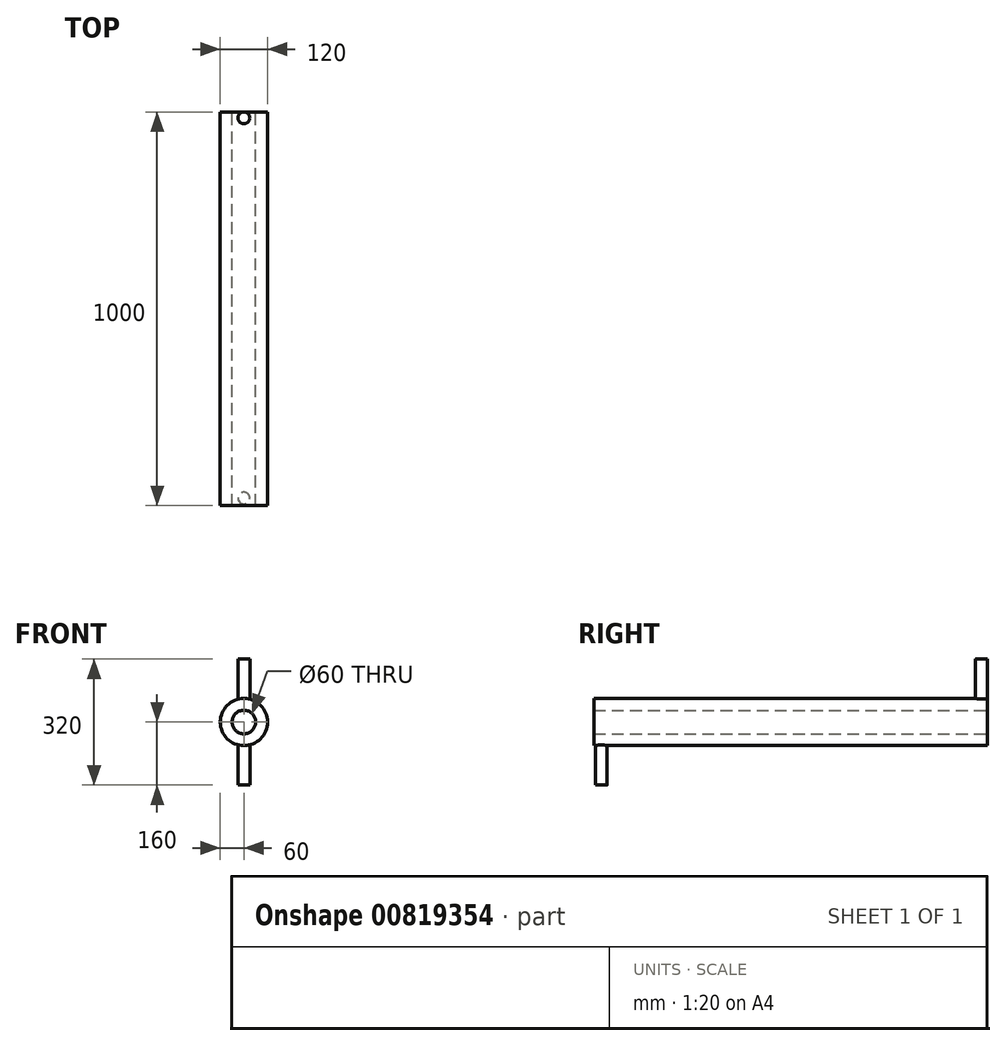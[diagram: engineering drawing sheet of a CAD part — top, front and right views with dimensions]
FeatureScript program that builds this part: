
annotation { "Feature Type Name" : "Feature", "Feature Type Description" : "" }
export const myFeature = defineFeature(function(context is Context, id is Id, definition is map)
    precondition{}
    {
        {
            var Q0;
            Q0=qCreatedBy(makeId("Front.planeOp"),FACE);
            var sketch = newSketch(context, id + "F0", { "sketchPlane" : qUnion([Q0])});
            skCircle(sketch, "E0", {"center": v(0, 0) * mm, "radius": 60 * mm});
            skCircle(sketch, "E1", {"center": v(0, 0) * mm, "radius": 30 * mm});
            skSolve(sketch);
        }
        {
            var Q0;
            Q0=makeQuery(id+"F0.imprint","IMPRINT",FACE,{"disambiguationData":[TD([[makeQuery(id+"F0.imprint","IMPRINT",EDGE,{"derivedFrom":sQuery(id+"F0.wireOp",EDGE,"E0")}),1.0]])]});
            extrude(context, id + "F1", {"entities" : qUnion([Q0]), "depth" : 1000 * mm, "offsetDistance" : 25 * mm});
        }
        {
            var Q0;
            Q0=qCreatedBy(makeId("Top.planeOp"),FACE);
            cPlane(context, id + "F2", {"entities" : qUnion([Q0]), "cplaneType" : CPlaneType.OFFSET, "offset" : 60 * mm, "width" : 150 * mm, "height" : 150 * mm});
        }
        {
            var Q0;
            Q0=qCreatedBy(id+"F2.planeOp",FACE);
            var sketch = newSketch(context, id + "F3", { "sketchPlane" : qUnion([Q0])});
            skCircle(sketch, "E2", {"center": v(0, -15) * mm, "radius": 15 * mm});
            skSolve(sketch);
        }
        {
            var Q0;
            Q0=makeQuery(id+"F3.imprint","IMPRINT",FACE,{"disambiguationData":[TD([[makeQuery(id+"F3.imprint","IMPRINT",EDGE,{"derivedFrom":sQuery(id+"F3.wireOp",EDGE,"E2")}),1.0]])]});
            var Q1;
            Q1=sQuery(id+"F3.wireOp",EDGE,"E2");
            extrude(context, id + "F4", {"entities" : qUnion([Q0]), "operationType" : NewBodyOperationType.ADD, "surfaceEntities" : qUnion([Q1]), "depth" : 100 * mm, "offsetDistance" : 25 * mm, "hasSecondDirection" : true, "secondDirectionOppositeDirection" : true, "secondDirectionDepth" : 7 * mm});
        }
        {
            var Q0;
            Q0=qCreatedBy(makeId("Top.planeOp"),FACE);
            cPlane(context, id + "F5", {"entities" : qUnion([Q0]), "cplaneType" : CPlaneType.OFFSET, "offset" : 60 * mm, "oppositeDirection" : true, "width" : 150 * mm, "height" : 150 * mm});
        }
        {
            var Q0;
            Q0=qCreatedBy(id+"F5.planeOp",FACE);
            var sketch = newSketch(context, id + "F6", { "sketchPlane" : qUnion([Q0])});
            skCircle(sketch, "E3", {"center": v(0, -981) * mm, "radius": 15 * mm});
            skSolve(sketch);
        }
        {
            var Q0;
            Q0=makeQuery(id+"F6.imprint","IMPRINT",FACE,{"disambiguationData":[TD([[makeQuery(id+"F6.imprint","IMPRINT",EDGE,{"derivedFrom":sQuery(id+"F6.wireOp",EDGE,"E3")}),1.0]])]});
            var Q1;
            Q1=sQuery(id+"F6.wireOp",EDGE,"E3");
            extrude(context, id + "F7", {"entities" : qUnion([Q0]), "operationType" : NewBodyOperationType.ADD, "surfaceEntities" : qUnion([Q1]), "oppositeDirection" : true, "depth" : 100 * mm, "offsetDistance" : 25 * mm, "hasSecondDirection" : true, "secondDirectionOppositeDirection" : false, "secondDirectionDepth" : 7 * mm});
        }
    });
